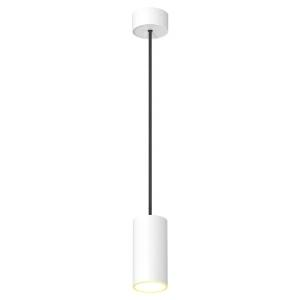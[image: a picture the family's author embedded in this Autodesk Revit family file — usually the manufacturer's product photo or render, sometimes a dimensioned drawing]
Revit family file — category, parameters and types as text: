
# Revit family: hangover_810-0470
name_source: partatom
category: Leuchten
revit_build: Autodesk Revit 2018 (Build: 20190510_1515(x64)
units: mm (PartAtom-declared; Revit-internal decimal feet)

## family parameters
Basisbauteil = Fläche
Beim Laden mit Abzugskörper schneiden = Nein
Bemaßung runder Anschluss = Durchmesser verwenden
Gemeinsam genutzt = Nein
Lichtquelle = Nein
Raumberechnungspunkt = Nein
Teiletyp = Normal

## types (1)
- 810-0470-H30-K18
    Beschreibung = HANGOVER
    CIE Flux Codes = 90 97 99 100 88
    Color Rendering = 1A/90…99
    Color Temperature = 3000K
    Height = 150 mm
    Hersteller = Prolicht
    Lamp Light Flux = 967
    Lamp Power = 9.8 W
    Lamp count = 1
    Lampe = 1 x LED
    Length = 75 mm
    Luminous efficacy = 87 lm/W
    ModVariant = Nein
    Modell = 810-0470-h30-k18-l00
    Mounting Place = Ceiling
    Mounting Type = Pendant
    Number of Poles = 1
    OnlyDefault = Ja
    Power Factor = 1
    Product Name = HANGOVER
    Product group = Suspended spotlights
    ProductGroupID = 942
    Protection Class = Protection class
    Protection Degree = Degree of protection
    RLX_Detail_Level = 1
    Scheinlast = 10 VA
    Socket = socket
    Standby Power = 0 W
    System Light Flux = 857 lm
    System Power = 10 W
    Typenbild = 410-7550.jpg
    Typenkommentare = LED COLOUR DIR 2700 K (27),REFLECTOR 18° (18),SHINE RING ABSICHTLICH_LEER (00)
    URL = http://prolicht.at
    VarID = 810-0470-h30-k18-l00
    Voltage = 0 V
    Vorgabe-Ansicht = 1800 mm
    Weight = 0.00 kg
    Width = 0 mm  [stored 0 ft]

note: [stored X ft] marks values corroborated as IEEE doubles in the binary element streams (Revit-internal decimal feet)

## geometry (parser evidence)
native form markers: Blend x4, Sweep x9
no freeform markers — native parametric forms only
